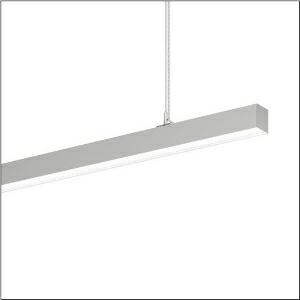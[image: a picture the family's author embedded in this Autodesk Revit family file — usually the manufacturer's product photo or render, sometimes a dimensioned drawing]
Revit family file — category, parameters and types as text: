
# Revit family: silica_r__21_51mx33dc4dsb_9471
name_source: partatom
category: Lighting Fixtures
units: mm (PartAtom-declared; Revit-internal decimal feet)

## family parameters
Cut with Voids When Loaded = No
Host = Face
Light Source = No
Part Type = Normal
Room Calculation Point = No
Round Connector Dimension = Use Diameter
Shared = No

## types (1)
- --- (1 x LED, 14790 lm, 93.9 W, 4000K)
    Apparent Load = 94 VA
    CIE Flux Codes = 78 96 99 55 100
    Color Rendering = 80
    Color Temperature = 4000K
    Default Elevation = 1800 mm
    Description = Silica® 21, office luminaire, primary optical cover: prismatic diffuser, of PMMA, CAT 2 (L<= 3000cd/m²), light emission: direct/indirect distribution, primary light characteristic: symmetric, installation type: suspended mounting, LED, rated luminous flux: 14.790lm, luminous efficacy: 158lm/W, light colour: 840, colour temperature: 4000K, control gear: DALI 2, with terminal, 3+2-pole, max. 2.5mm², mains connection: 220..240V, AC, 50/60Hz, rated input power: 93.9W, luminaire housing, of aluminium, metallic grey (RAL 9006), length: 3.004mm, width: 53mm, height: 53mm, protection rating (complete): IP20, insulation class (complete): insulation class I (protective earthing), certification: CE, permissible operating ambient temperature: 0..+35°C, standard: EN 50419, packaging unit: 1 piece
    Height = 53 mm
    Lamp = 1 x LED
    Lamp Light Flux = 14790 lm
    Lamp Power = 93.9 W
    Lamp count = 1
    Length = 3004 mm
    Luminous efficacy = 158 lm/W
    Manufacturer = Siteco
    ModVariant = No
    Model = 51MX33DC4DSB
    Mounting Place = Ceiling
    Mounting Type = Pendant
    Number of Poles = 1
    OnlyDefault = Yes
    Power Factor = 1
    Product Name = Silica® 21
    Product group = office luminaire | ceiling pendant
    ProductGroupID = 903
    Protection Class = Protection class I
    Protection Degree = IP 20
    RLX_Detail_Level = 1
    RLX_Emergency_Light_Flux = 0 lm
    RLX_Emergency_Type = 0
    RLX_Emergency_Type_DB = No
    RlxData = <blob elided: 23453 chars, md5=98d57391>
    Socket = socket
    Standby Power = 0 W
    System Light Flux = 14790 lm
    System Power = 94 W
    Type Comments = factory setting: luminous flux: 100 % | dim-lin: 254 | 323 mA
    Type Image = l_1335864.jpg
    URL = http://relux.com
    VarID = @adj_140025
    Voltage = 0 V
    Weight = 0.00 kg
    Width = 53 mm

## geometry (parser evidence)
native form markers: Blend x4, Sweep x12
no freeform markers — native parametric forms only
